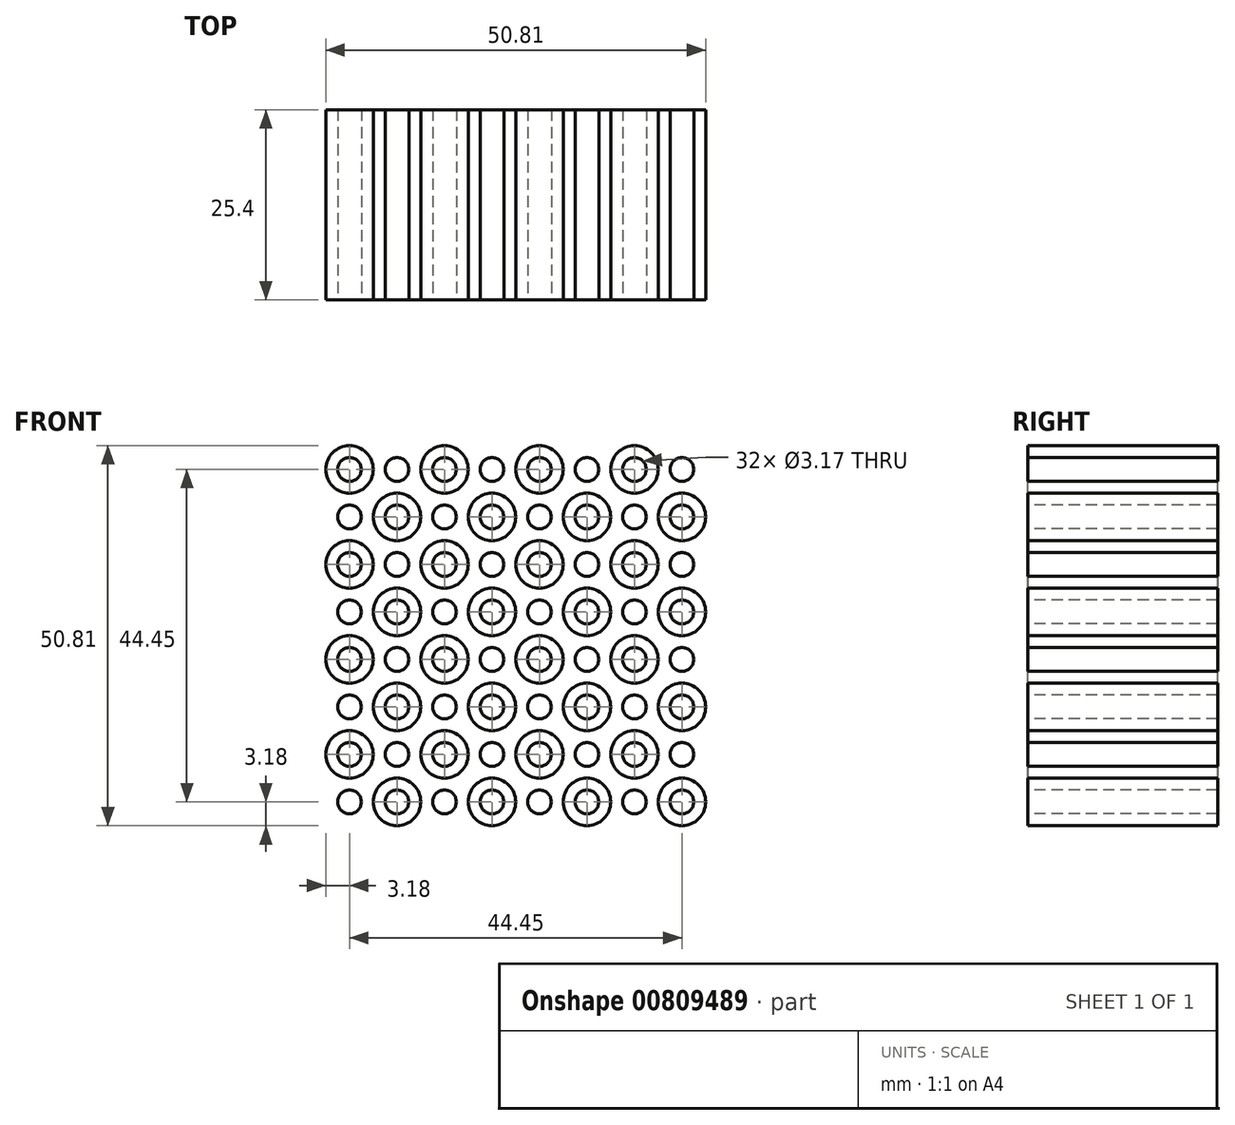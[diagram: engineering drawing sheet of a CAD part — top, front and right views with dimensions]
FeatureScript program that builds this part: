
annotation { "Feature Type Name" : "Feature", "Feature Type Description" : "" }
export const myFeature = defineFeature(function(context is Context, id is Id, definition is map)
    precondition{}
    {
        {
            var Q0;
            Q0=qCreatedBy(makeId("Front.planeOp"),FACE);
            var sketch = newSketch(context, id + "F0", { "sketchPlane" : qUnion([Q0])});
            skCircle(sketch, "E0", {"center": v(0, 0) * mm, "radius": 1.59 * mm});
            skCircle(sketch, "E1", {"center": v(0, 0) * mm, "radius": 3.18 * mm});
            skLineSegment(sketch, "E2.bottom", {"start": v(-3.18, 3.18) * mm, "end": v(3.18, 3.18) * mm});
            skLineSegment(sketch, "E2.top", {"start": v(-3.17, -3.18) * mm, "end": v(3.18, -3.18) * mm});
            skLineSegment(sketch, "E2.left", {"start": v(-3.18, 3.17) * mm, "end": v(-3.18, -3.18) * mm});
            skLineSegment(sketch, "E2.right", {"start": v(3.18, 3.18) * mm, "end": v(3.18, -3.18) * mm});
            skCircle(sketch, "E3.MirrorC", {"center": v(6.35, 0) * mm, "radius": 3.18 * mm});
            skCircle(sketch, "E4.MirrorC", {"center": v(6.35, 0) * mm, "radius": 1.59 * mm});
            skLineSegment(sketch, "E5.MirrorCS", {"start": v(9.53, 3.18) * mm, "end": v(3.17, 3.18) * mm});
            skLineSegment(sketch, "E6.MirrorCS", {"start": v(9.53, 3.18) * mm, "end": v(9.53, -3.17) * mm});
            skLineSegment(sketch, "E7.MirrorCS", {"start": v(9.53, -3.17) * mm, "end": v(3.17, -3.18) * mm});
            skCircle(sketch, "E8.MirrorC", {"center": v(6.35, -6.35) * mm, "radius": 3.18 * mm});
            skCircle(sketch, "E9.MirrorC", {"center": v(0, -6.35) * mm, "radius": 3.18 * mm});
            skCircle(sketch, "E10.MirrorC", {"center": v(0, -6.35) * mm, "radius": 1.59 * mm});
            skLineSegment(sketch, "E11.MirrorCS", {"start": v(3.18, -9.53) * mm, "end": v(3.18, -3.18) * mm});
            skCircle(sketch, "E12.MirrorC", {"center": v(6.35, -6.35) * mm, "radius": 1.59 * mm});
            skCircle(sketch, "E13.MirrorC", {"center": v(-6.35, 0) * mm, "radius": 1.59 * mm});
            skCircle(sketch, "E14.MirrorC", {"center": v(-6.35, 0) * mm, "radius": 3.18 * mm});
            skCircle(sketch, "E15.MirrorC", {"center": v(-12.7, 0) * mm, "radius": 3.18 * mm});
            skCircle(sketch, "E16.MirrorC", {"center": v(-12.7, 0) * mm, "radius": 1.59 * mm});
            skLineSegment(sketch, "E17.MirrorCS", {"start": v(-9.53, 3.17) * mm, "end": v(-9.53, -3.18) * mm});
            skLineSegment(sketch, "E18.MirrorCS", {"start": v(-3.18, 3.18) * mm, "end": v(-9.53, 3.17) * mm});
            skCircle(sketch, "E19.MirrorC", {"center": v(-6.35, -6.35) * mm, "radius": 1.59 * mm});
            skCircle(sketch, "E20.MirrorC", {"center": v(-6.35, -6.35) * mm, "radius": 3.18 * mm});
            skCircle(sketch, "E21.MirrorC", {"center": v(-12.7, -6.35) * mm, "radius": 1.59 * mm});
            skCircle(sketch, "E22.MirrorC", {"center": v(-12.7, -6.35) * mm, "radius": 3.18 * mm});
            skLineSegment(sketch, "E23.MirrorCS", {"start": v(-3.18, -9.53) * mm, "end": v(3.18, -9.53) * mm});
            skCircle(sketch, "E24.MirrorC", {"center": v(-12.7, -19.05) * mm, "radius": 3.18 * mm});
            skCircle(sketch, "E25.MirrorC", {"center": v(-12.7, -19.05) * mm, "radius": 1.59 * mm});
            skCircle(sketch, "E26.MirrorC", {"center": v(-6.35, -19.05) * mm, "radius": 1.59 * mm});
            skCircle(sketch, "E27.MirrorC", {"center": v(-6.35, -19.05) * mm, "radius": 3.18 * mm});
            skCircle(sketch, "E28.MirrorC", {"center": v(0, -19.05) * mm, "radius": 3.18 * mm});
            skCircle(sketch, "E29.MirrorC", {"center": v(0, -19.05) * mm, "radius": 1.59 * mm});
            skCircle(sketch, "E30.MirrorC", {"center": v(6.35, -19.05) * mm, "radius": 3.18 * mm});
            skCircle(sketch, "E31.MirrorC", {"center": v(6.35, -19.05) * mm, "radius": 1.59 * mm});
            skLineSegment(sketch, "E32.MirrorCS", {"start": v(-3.18, -22.23) * mm, "end": v(3.18, -22.23) * mm});
            skCircle(sketch, "E33.MirrorC", {"center": v(-12.7, -12.7) * mm, "radius": 1.59 * mm});
            skCircle(sketch, "E34.MirrorC", {"center": v(-12.7, -12.7) * mm, "radius": 3.18 * mm});
            skCircle(sketch, "E35.MirrorC", {"center": v(-6.35, -12.7) * mm, "radius": 3.18 * mm});
            skCircle(sketch, "E36.MirrorC", {"center": v(-6.35, -12.7) * mm, "radius": 1.59 * mm});
            skCircle(sketch, "E37.MirrorC", {"center": v(0, -12.7) * mm, "radius": 1.59 * mm});
            skCircle(sketch, "E38.MirrorC", {"center": v(0, -12.7) * mm, "radius": 3.18 * mm});
            skCircle(sketch, "E39.MirrorC", {"center": v(6.35, -12.7) * mm, "radius": 3.18 * mm});
            skCircle(sketch, "E40.MirrorC", {"center": v(6.35, -12.7) * mm, "radius": 1.59 * mm});
            skCircle(sketch, "E41.MirrorC", {"center": v(31.75, 0) * mm, "radius": 3.18 * mm});
            skCircle(sketch, "E42.MirrorC", {"center": v(31.75, 0) * mm, "radius": 1.59 * mm});
            skCircle(sketch, "E43.MirrorC", {"center": v(25.4, 0) * mm, "radius": 1.59 * mm});
            skCircle(sketch, "E44.MirrorC", {"center": v(25.4, 0) * mm, "radius": 3.18 * mm});
            skCircle(sketch, "E45.MirrorC", {"center": v(19.05, 0) * mm, "radius": 3.18 * mm});
            skCircle(sketch, "E46.MirrorC", {"center": v(19.05, 0) * mm, "radius": 1.59 * mm});
            skCircle(sketch, "E47.MirrorC", {"center": v(12.7, 0) * mm, "radius": 3.18 * mm});
            skCircle(sketch, "E48.MirrorC", {"center": v(12.7, 0) * mm, "radius": 1.59 * mm});
            skCircle(sketch, "E49.MirrorC", {"center": v(12.7, -6.35) * mm, "radius": 1.59 * mm});
            skCircle(sketch, "E50.MirrorC", {"center": v(12.7, -6.35) * mm, "radius": 3.18 * mm});
            skCircle(sketch, "E51.MirrorC", {"center": v(19.05, -6.35) * mm, "radius": 3.18 * mm});
            skCircle(sketch, "E52.MirrorC", {"center": v(19.05, -6.35) * mm, "radius": 1.59 * mm});
            skCircle(sketch, "E53.MirrorC", {"center": v(25.4, -12.7) * mm, "radius": 3.18 * mm});
            skCircle(sketch, "E54.MirrorC", {"center": v(25.4, -12.7) * mm, "radius": 1.59 * mm});
            skCircle(sketch, "E55.MirrorC", {"center": v(25.4, -6.35) * mm, "radius": 3.18 * mm});
            skCircle(sketch, "E56.MirrorC", {"center": v(25.4, -6.35) * mm, "radius": 1.59 * mm});
            skCircle(sketch, "E57.MirrorC", {"center": v(31.75, -6.35) * mm, "radius": 1.59 * mm});
            skCircle(sketch, "E58.MirrorC", {"center": v(31.75, -6.35) * mm, "radius": 3.18 * mm});
            skCircle(sketch, "E59.MirrorC", {"center": v(31.75, -12.7) * mm, "radius": 3.18 * mm});
            skCircle(sketch, "E60.MirrorC", {"center": v(31.75, -12.7) * mm, "radius": 1.59 * mm});
            skCircle(sketch, "E61.MirrorC", {"center": v(31.75, -19.05) * mm, "radius": 3.18 * mm});
            skCircle(sketch, "E62.MirrorC", {"center": v(31.75, -19.05) * mm, "radius": 1.59 * mm});
            skCircle(sketch, "E63.MirrorC", {"center": v(25.4, -19.05) * mm, "radius": 1.59 * mm});
            skCircle(sketch, "E64.MirrorC", {"center": v(25.4, -19.05) * mm, "radius": 3.18 * mm});
            skCircle(sketch, "E65.MirrorC", {"center": v(19.05, -19.05) * mm, "radius": 3.18 * mm});
            skCircle(sketch, "E66.MirrorC", {"center": v(19.05, -19.05) * mm, "radius": 1.59 * mm});
            skCircle(sketch, "E67.MirrorC", {"center": v(12.7, -19.05) * mm, "radius": 3.18 * mm});
            skCircle(sketch, "E68.MirrorC", {"center": v(12.7, -19.05) * mm, "radius": 1.59 * mm});
            skCircle(sketch, "E69.MirrorC", {"center": v(12.7, -12.7) * mm, "radius": 3.18 * mm});
            skCircle(sketch, "E70.MirrorC", {"center": v(12.7, -12.7) * mm, "radius": 1.59 * mm});
            skCircle(sketch, "E71.MirrorC", {"center": v(19.05, -12.7) * mm, "radius": 3.18 * mm});
            skCircle(sketch, "E72.MirrorC", {"center": v(19.05, -12.7) * mm, "radius": 1.59 * mm});
            skCircle(sketch, "E73.MirrorC", {"center": v(-12.7, 6.35) * mm, "radius": 3.18 * mm});
            skCircle(sketch, "E74.MirrorC", {"center": v(-12.7, 6.35) * mm, "radius": 1.59 * mm});
            skCircle(sketch, "E75.MirrorC", {"center": v(31.75, 12.7) * mm, "radius": 3.18 * mm});
            skCircle(sketch, "E76.MirrorC", {"center": v(19.05, 19.05) * mm, "radius": 3.18 * mm});
            skCircle(sketch, "E77.MirrorC", {"center": v(12.7, 12.7) * mm, "radius": 1.59 * mm});
            skCircle(sketch, "E78.MirrorC", {"center": v(-6.35, 25.4) * mm, "radius": 3.18 * mm});
            skCircle(sketch, "E79.MirrorC", {"center": v(-6.35, 19.05) * mm, "radius": 1.59 * mm});
            skCircle(sketch, "E80.MirrorC", {"center": v(-6.35, 12.7) * mm, "radius": 3.18 * mm});
            skCircle(sketch, "E81.MirrorC", {"center": v(-6.35, 19.05) * mm, "radius": 3.18 * mm});
            skCircle(sketch, "E82.MirrorC", {"center": v(-12.7, 12.7) * mm, "radius": 3.18 * mm});
            skCircle(sketch, "E83.MirrorC", {"center": v(-6.35, 12.7) * mm, "radius": 1.59 * mm});
            skCircle(sketch, "E84.MirrorC", {"center": v(0, 19.05) * mm, "radius": 1.59 * mm});
            skCircle(sketch, "E85.MirrorC", {"center": v(0, 12.7) * mm, "radius": 1.59 * mm});
            skCircle(sketch, "E86.MirrorC", {"center": v(19.05, 12.7) * mm, "radius": 1.59 * mm});
            skCircle(sketch, "E87.MirrorC", {"center": v(0, 12.7) * mm, "radius": 3.18 * mm});
            skCircle(sketch, "E88.MirrorC", {"center": v(6.35, 19.05) * mm, "radius": 3.18 * mm});
            skCircle(sketch, "E89.MirrorC", {"center": v(12.7, 12.7) * mm, "radius": 3.18 * mm});
            skCircle(sketch, "E90.MirrorC", {"center": v(25.4, 12.7) * mm, "radius": 1.59 * mm});
            skCircle(sketch, "E91.MirrorC", {"center": v(6.35, 12.7) * mm, "radius": 1.59 * mm});
            skCircle(sketch, "E92.MirrorC", {"center": v(-12.7, 19.05) * mm, "radius": 1.59 * mm});
            skCircle(sketch, "E93.MirrorC", {"center": v(-12.7, 25.4) * mm, "radius": 1.59 * mm});
            skCircle(sketch, "E94.MirrorC", {"center": v(-12.7, 25.4) * mm, "radius": 3.18 * mm});
            skCircle(sketch, "E95.MirrorC", {"center": v(-12.7, 19.05) * mm, "radius": 3.18 * mm});
            skCircle(sketch, "E96.MirrorC", {"center": v(-12.7, 12.7) * mm, "radius": 1.59 * mm});
            skCircle(sketch, "E97.MirrorC", {"center": v(-6.35, 25.4) * mm, "radius": 1.59 * mm});
            skCircle(sketch, "E98.MirrorC", {"center": v(-6.35, 6.35) * mm, "radius": 3.18 * mm});
            skCircle(sketch, "E99.MirrorC", {"center": v(-6.35, 6.35) * mm, "radius": 1.59 * mm});
            skCircle(sketch, "E100.MirrorC", {"center": v(0, 6.35) * mm, "radius": 1.59 * mm});
            skCircle(sketch, "E101.MirrorC", {"center": v(0, 6.35) * mm, "radius": 3.18 * mm});
            skCircle(sketch, "E102.MirrorC", {"center": v(0, 19.05) * mm, "radius": 3.18 * mm});
            skCircle(sketch, "E103.MirrorC", {"center": v(0, 25.4) * mm, "radius": 3.18 * mm});
            skCircle(sketch, "E104.MirrorC", {"center": v(0, 25.4) * mm, "radius": 1.59 * mm});
            skCircle(sketch, "E105.MirrorC", {"center": v(6.35, 25.4) * mm, "radius": 3.18 * mm});
            skCircle(sketch, "E106.MirrorC", {"center": v(6.35, 25.4) * mm, "radius": 1.59 * mm});
            skCircle(sketch, "E107.MirrorC", {"center": v(6.35, 19.05) * mm, "radius": 1.59 * mm});
            skCircle(sketch, "E108.MirrorC", {"center": v(6.35, 12.7) * mm, "radius": 3.18 * mm});
            skCircle(sketch, "E109.MirrorC", {"center": v(6.35, 6.35) * mm, "radius": 3.18 * mm});
            skCircle(sketch, "E110.MirrorC", {"center": v(6.35, 6.35) * mm, "radius": 1.59 * mm});
            skCircle(sketch, "E111.MirrorC", {"center": v(12.7, 6.35) * mm, "radius": 3.18 * mm});
            skCircle(sketch, "E112.MirrorC", {"center": v(12.7, 6.35) * mm, "radius": 1.59 * mm});
            skCircle(sketch, "E113.MirrorC", {"center": v(25.4, 12.7) * mm, "radius": 3.18 * mm});
            skCircle(sketch, "E114.MirrorC", {"center": v(19.05, 12.7) * mm, "radius": 3.18 * mm});
            skCircle(sketch, "E115.MirrorC", {"center": v(19.05, 6.35) * mm, "radius": 1.59 * mm});
            skCircle(sketch, "E116.MirrorC", {"center": v(19.05, 6.35) * mm, "radius": 3.18 * mm});
            skCircle(sketch, "E117.MirrorC", {"center": v(25.4, 6.35) * mm, "radius": 3.18 * mm});
            skCircle(sketch, "E118.MirrorC", {"center": v(25.4, 6.35) * mm, "radius": 1.59 * mm});
            skCircle(sketch, "E119.MirrorC", {"center": v(31.75, 6.35) * mm, "radius": 3.18 * mm});
            skCircle(sketch, "E120.MirrorC", {"center": v(31.75, 6.35) * mm, "radius": 1.59 * mm});
            skCircle(sketch, "E121.MirrorC", {"center": v(31.75, 25.4) * mm, "radius": 3.18 * mm});
            skCircle(sketch, "E122.MirrorC", {"center": v(25.4, 25.4) * mm, "radius": 3.18 * mm});
            skCircle(sketch, "E123.MirrorC", {"center": v(19.05, 25.4) * mm, "radius": 3.18 * mm});
            skCircle(sketch, "E124.MirrorC", {"center": v(12.7, 25.4) * mm, "radius": 3.18 * mm});
            skCircle(sketch, "E125.MirrorC", {"center": v(12.7, 25.4) * mm, "radius": 1.59 * mm});
            skCircle(sketch, "E126.MirrorC", {"center": v(19.05, 25.4) * mm, "radius": 1.59 * mm});
            skCircle(sketch, "E127.MirrorC", {"center": v(25.4, 25.4) * mm, "radius": 1.59 * mm});
            skCircle(sketch, "E128.MirrorC", {"center": v(31.75, 25.4) * mm, "radius": 1.59 * mm});
            skCircle(sketch, "E129.MirrorC", {"center": v(12.7, 19.05) * mm, "radius": 3.18 * mm});
            skCircle(sketch, "E130.MirrorC", {"center": v(12.7, 19.05) * mm, "radius": 1.59 * mm});
            skCircle(sketch, "E131.MirrorC", {"center": v(19.05, 19.05) * mm, "radius": 1.59 * mm});
            skCircle(sketch, "E132.MirrorC", {"center": v(25.4, 19.05) * mm, "radius": 3.18 * mm});
            skCircle(sketch, "E133.MirrorC", {"center": v(31.75, 19.05) * mm, "radius": 3.18 * mm});
            skCircle(sketch, "E134.MirrorC", {"center": v(31.75, 12.7) * mm, "radius": 1.59 * mm});
            skCircle(sketch, "E135.MirrorC", {"center": v(31.75, 19.05) * mm, "radius": 1.59 * mm});
            skCircle(sketch, "E136.MirrorC", {"center": v(25.4, 19.05) * mm, "radius": 1.59 * mm});
            skSolve(sketch);
        }
        {
            var Q0;
            Q0=makeQuery(id+"F0.imprint","IMPRINT",FACE,{"disambiguationData":[TD([[makeQuery(id+"F0.imprint","IMPRINT",EDGE,{"derivedFrom":sQuery(id+"F0.wireOp",EDGE,"E97.MirrorC")}),1.0]])]});
            var Q1;
            Q1=makeQuery(id+"F0.imprint","IMPRINT",FACE,{"disambiguationData":[TD([[makeQuery(id+"F0.imprint","IMPRINT",EDGE,{"derivedFrom":sQuery(id+"F0.wireOp",EDGE,"E104.MirrorC")}),-1.0]])]});
            var Q2;
            Q2=makeQuery(id+"F0.imprint","IMPRINT",FACE,{"disambiguationData":[TD([[makeQuery(id+"F0.imprint","IMPRINT",EDGE,{"derivedFrom":sQuery(id+"F0.wireOp",EDGE,"E106.MirrorC")}),1.0]])]});
            var Q3;
            Q3=makeQuery(id+"F0.imprint","IMPRINT",FACE,{"disambiguationData":[TD([[makeQuery(id+"F0.imprint","IMPRINT",EDGE,{"derivedFrom":sQuery(id+"F0.wireOp",EDGE,"E125.MirrorC")}),-1.0]])]});
            var Q4;
            Q4=makeQuery(id+"F0.imprint","IMPRINT",FACE,{"disambiguationData":[TD([[makeQuery(id+"F0.imprint","IMPRINT",EDGE,{"derivedFrom":sQuery(id+"F0.wireOp",EDGE,"E93.MirrorC")}),-1.0]])]});
            var Q5;
            Q5=makeQuery(id+"F0.imprint","IMPRINT",FACE,{"disambiguationData":[TD([[makeQuery(id+"F0.imprint","IMPRINT",EDGE,{"derivedFrom":sQuery(id+"F0.wireOp",EDGE,"E126.MirrorC")}),1.0]])]});
            var Q6;
            Q6=makeQuery(id+"F0.imprint","IMPRINT",FACE,{"disambiguationData":[TD([[makeQuery(id+"F0.imprint","IMPRINT",EDGE,{"derivedFrom":sQuery(id+"F0.wireOp",EDGE,"E127.MirrorC")}),-1.0]])]});
            var Q7;
            Q7=makeQuery(id+"F0.imprint","IMPRINT",FACE,{"disambiguationData":[TD([[makeQuery(id+"F0.imprint","IMPRINT",EDGE,{"derivedFrom":sQuery(id+"F0.wireOp",EDGE,"E128.MirrorC")}),1.0]])]});
            var Q8;
            Q8=makeQuery(id+"F0.imprint","IMPRINT",FACE,{"disambiguationData":[TD([[makeQuery(id+"F0.imprint","IMPRINT",EDGE,{"derivedFrom":sQuery(id+"F0.wireOp",EDGE,"E135.MirrorC")}),-1.0]])]});
            var Q9;
            Q9=makeQuery(id+"F0.imprint","IMPRINT",FACE,{"disambiguationData":[TD([[makeQuery(id+"F0.imprint","IMPRINT",EDGE,{"derivedFrom":sQuery(id+"F0.wireOp",EDGE,"E136.MirrorC")}),1.0]])]});
            var Q10;
            Q10=makeQuery(id+"F0.imprint","IMPRINT",FACE,{"disambiguationData":[TD([[makeQuery(id+"F0.imprint","IMPRINT",EDGE,{"derivedFrom":sQuery(id+"F0.wireOp",EDGE,"E131.MirrorC")}),-1.0]])]});
            var Q11;
            Q11=makeQuery(id+"F0.imprint","IMPRINT",FACE,{"disambiguationData":[TD([[makeQuery(id+"F0.imprint","IMPRINT",EDGE,{"derivedFrom":sQuery(id+"F0.wireOp",EDGE,"E130.MirrorC")}),1.0]])]});
            var Q12;
            Q12=makeQuery(id+"F0.imprint","IMPRINT",FACE,{"disambiguationData":[TD([[makeQuery(id+"F0.imprint","IMPRINT",EDGE,{"derivedFrom":sQuery(id+"F0.wireOp",EDGE,"E107.MirrorC")}),-1.0]])]});
            var Q13;
            Q13=makeQuery(id+"F0.imprint","IMPRINT",FACE,{"disambiguationData":[TD([[makeQuery(id+"F0.imprint","IMPRINT",EDGE,{"derivedFrom":sQuery(id+"F0.wireOp",EDGE,"E84.MirrorC")}),1.0]])]});
            var Q14;
            Q14=makeQuery(id+"F0.imprint","IMPRINT",FACE,{"disambiguationData":[TD([[makeQuery(id+"F0.imprint","IMPRINT",EDGE,{"derivedFrom":sQuery(id+"F0.wireOp",EDGE,"E79.MirrorC")}),-1.0]])]});
            var Q15;
            Q15=makeQuery(id+"F0.imprint","IMPRINT",FACE,{"disambiguationData":[TD([[makeQuery(id+"F0.imprint","IMPRINT",EDGE,{"derivedFrom":sQuery(id+"F0.wireOp",EDGE,"E92.MirrorC")}),1.0]])]});
            var Q16;
            Q16=makeQuery(id+"F0.imprint","IMPRINT",FACE,{"disambiguationData":[TD([[makeQuery(id+"F0.imprint","IMPRINT",EDGE,{"derivedFrom":sQuery(id+"F0.wireOp",EDGE,"E96.MirrorC")}),-1.0]])]});
            var Q17;
            Q17=makeQuery(id+"F0.imprint","IMPRINT",FACE,{"disambiguationData":[TD([[makeQuery(id+"F0.imprint","IMPRINT",EDGE,{"derivedFrom":sQuery(id+"F0.wireOp",EDGE,"E83.MirrorC")}),1.0]])]});
            var Q18;
            Q18=makeQuery(id+"F0.imprint","IMPRINT",FACE,{"disambiguationData":[TD([[makeQuery(id+"F0.imprint","IMPRINT",EDGE,{"derivedFrom":sQuery(id+"F0.wireOp",EDGE,"E91.MirrorC")}),1.0]])]});
            var Q19;
            Q19=makeQuery(id+"F0.imprint","IMPRINT",FACE,{"disambiguationData":[TD([[makeQuery(id+"F0.imprint","IMPRINT",EDGE,{"derivedFrom":sQuery(id+"F0.wireOp",EDGE,"E77.MirrorC")}),-1.0]])]});
            var Q20;
            Q20=makeQuery(id+"F0.imprint","IMPRINT",FACE,{"disambiguationData":[TD([[makeQuery(id+"F0.imprint","IMPRINT",EDGE,{"derivedFrom":sQuery(id+"F0.wireOp",EDGE,"E86.MirrorC")}),1.0]])]});
            var Q21;
            Q21=makeQuery(id+"F0.imprint","IMPRINT",FACE,{"disambiguationData":[TD([[makeQuery(id+"F0.imprint","IMPRINT",EDGE,{"derivedFrom":sQuery(id+"F0.wireOp",EDGE,"E90.MirrorC")}),-1.0]])]});
            var Q22;
            Q22=makeQuery(id+"F0.imprint","IMPRINT",FACE,{"disambiguationData":[TD([[makeQuery(id+"F0.imprint","IMPRINT",EDGE,{"derivedFrom":sQuery(id+"F0.wireOp",EDGE,"E134.MirrorC")}),1.0]])]});
            var Q23;
            Q23=makeQuery(id+"F0.imprint","IMPRINT",FACE,{"disambiguationData":[TD([[makeQuery(id+"F0.imprint","IMPRINT",EDGE,{"derivedFrom":sQuery(id+"F0.wireOp",EDGE,"E118.MirrorC")}),1.0]])]});
            var Q24;
            Q24=makeQuery(id+"F0.imprint","IMPRINT",FACE,{"disambiguationData":[TD([[makeQuery(id+"F0.imprint","IMPRINT",EDGE,{"derivedFrom":sQuery(id+"F0.wireOp",EDGE,"E115.MirrorC")}),-1.0]])]});
            var Q25;
            Q25=makeQuery(id+"F0.imprint","IMPRINT",FACE,{"disambiguationData":[TD([[makeQuery(id+"F0.imprint","IMPRINT",EDGE,{"derivedFrom":sQuery(id+"F0.wireOp",EDGE,"E112.MirrorC")}),1.0]])]});
            var Q26;
            Q26=makeQuery(id+"F0.imprint","IMPRINT",FACE,{"disambiguationData":[TD([[makeQuery(id+"F0.imprint","IMPRINT",EDGE,{"derivedFrom":sQuery(id+"F0.wireOp",EDGE,"E110.MirrorC")}),-1.0]])]});
            var Q27;
            Q27=makeQuery(id+"F0.imprint","IMPRINT",FACE,{"disambiguationData":[TD([[makeQuery(id+"F0.imprint","IMPRINT",EDGE,{"derivedFrom":sQuery(id+"F0.wireOp",EDGE,"E100.MirrorC")}),1.0]])]});
            var Q28;
            Q28=makeQuery(id+"F0.imprint","IMPRINT",FACE,{"disambiguationData":[TD([[makeQuery(id+"F0.imprint","IMPRINT",EDGE,{"derivedFrom":sQuery(id+"F0.wireOp",EDGE,"E85.MirrorC")}),-1.0]])]});
            var Q29;
            Q29=makeQuery(id+"F0.imprint","IMPRINT",FACE,{"disambiguationData":[TD([[makeQuery(id+"F0.imprint","IMPRINT",EDGE,{"derivedFrom":sQuery(id+"F0.wireOp",EDGE,"E99.MirrorC")}),-1.0]])]});
            var Q30;
            Q30=makeQuery(id+"F0.imprint","IMPRINT",FACE,{"disambiguationData":[TD([[makeQuery(id+"F0.imprint","IMPRINT",EDGE,{"derivedFrom":sQuery(id+"F0.wireOp",EDGE,"E74.MirrorC")}),1.0]])]});
            var Q31;
            Q31=makeQuery(id+"F0.imprint","IMPRINT",FACE,{"disambiguationData":[TD([[makeQuery(id+"F0.imprint","IMPRINT",EDGE,{"derivedFrom":sQuery(id+"F0.wireOp",EDGE,"E120.MirrorC")}),-1.0]])]});
            var Q32;
            Q32=makeQuery(id+"F0.imprint","IMPRINT",FACE,{"disambiguationData":[TD([[makeQuery(id+"F0.imprint","IMPRINT",EDGE,{"derivedFrom":sQuery(id+"F0.wireOp",EDGE,"E42.MirrorC")}),1.0]])]});
            var Q33;
            Q33=makeQuery(id+"F0.imprint","IMPRINT",FACE,{"disambiguationData":[TD([[makeQuery(id+"F0.imprint","IMPRINT",EDGE,{"derivedFrom":sQuery(id+"F0.wireOp",EDGE,"E43.MirrorC")}),-1.0]])]});
            var Q34;
            Q34=makeQuery(id+"F0.imprint","IMPRINT",FACE,{"disambiguationData":[TD([[makeQuery(id+"F0.imprint","IMPRINT",EDGE,{"derivedFrom":sQuery(id+"F0.wireOp",EDGE,"E46.MirrorC")}),1.0]])]});
            var Q35;
            Q35=makeQuery(id+"F0.imprint","IMPRINT",FACE,{"disambiguationData":[TD([[makeQuery(id+"F0.imprint","IMPRINT",EDGE,{"derivedFrom":sQuery(id+"F0.wireOp",EDGE,"E48.MirrorC")}),-1.0]])]});
            var Q36;
            Q36=makeQuery(id+"F0.imprint","IMPRINT",FACE,{"disambiguationData":[TD([[makeQuery(id+"F0.imprint","IMPRINT",EDGE,{"derivedFrom":sQuery(id+"F0.wireOp",EDGE,"E4.MirrorC")}),1.0]])]});
            var Q37;
            Q37=makeQuery(id+"F0.imprint","IMPRINT",FACE,{"disambiguationData":[TD([[makeQuery(id+"F0.imprint","IMPRINT",EDGE,{"derivedFrom":sQuery(id+"F0.wireOp",EDGE,"E0")}),-1.0]])]});
            var Q38;
            Q38=makeQuery(id+"F0.imprint","IMPRINT",FACE,{"disambiguationData":[TD([[makeQuery(id+"F0.imprint","IMPRINT",EDGE,{"derivedFrom":sQuery(id+"F0.wireOp",EDGE,"E13.MirrorC")}),1.0]])]});
            var Q39;
            Q39=makeQuery(id+"F0.imprint","IMPRINT",FACE,{"disambiguationData":[TD([[makeQuery(id+"F0.imprint","IMPRINT",EDGE,{"derivedFrom":sQuery(id+"F0.wireOp",EDGE,"E16.MirrorC")}),-1.0]])]});
            var Q40;
            Q40=makeQuery(id+"F0.imprint","IMPRINT",FACE,{"disambiguationData":[TD([[makeQuery(id+"F0.imprint","IMPRINT",EDGE,{"derivedFrom":sQuery(id+"F0.wireOp",EDGE,"E21.MirrorC")}),1.0]])]});
            var Q41;
            Q41=makeQuery(id+"F0.imprint","IMPRINT",FACE,{"disambiguationData":[TD([[makeQuery(id+"F0.imprint","IMPRINT",EDGE,{"derivedFrom":sQuery(id+"F0.wireOp",EDGE,"E19.MirrorC")}),-1.0]])]});
            var Q42;
            Q42=makeQuery(id+"F0.imprint","IMPRINT",FACE,{"disambiguationData":[TD([[makeQuery(id+"F0.imprint","IMPRINT",EDGE,{"derivedFrom":sQuery(id+"F0.wireOp",EDGE,"E10.MirrorC")}),1.0]])]});
            var Q43;
            Q43=makeQuery(id+"F0.imprint","IMPRINT",FACE,{"disambiguationData":[TD([[makeQuery(id+"F0.imprint","IMPRINT",EDGE,{"derivedFrom":sQuery(id+"F0.wireOp",EDGE,"E12.MirrorC")}),-1.0]])]});
            var Q44;
            Q44=makeQuery(id+"F0.imprint","IMPRINT",FACE,{"disambiguationData":[TD([[makeQuery(id+"F0.imprint","IMPRINT",EDGE,{"derivedFrom":sQuery(id+"F0.wireOp",EDGE,"E49.MirrorC")}),1.0]])]});
            var Q45;
            Q45=makeQuery(id+"F0.imprint","IMPRINT",FACE,{"disambiguationData":[TD([[makeQuery(id+"F0.imprint","IMPRINT",EDGE,{"derivedFrom":sQuery(id+"F0.wireOp",EDGE,"E52.MirrorC")}),-1.0]])]});
            var Q46;
            Q46=makeQuery(id+"F0.imprint","IMPRINT",FACE,{"disambiguationData":[TD([[makeQuery(id+"F0.imprint","IMPRINT",EDGE,{"derivedFrom":sQuery(id+"F0.wireOp",EDGE,"E56.MirrorC")}),1.0]])]});
            var Q47;
            Q47=makeQuery(id+"F0.imprint","IMPRINT",FACE,{"disambiguationData":[TD([[makeQuery(id+"F0.imprint","IMPRINT",EDGE,{"derivedFrom":sQuery(id+"F0.wireOp",EDGE,"E57.MirrorC")}),-1.0]])]});
            var Q48;
            Q48=makeQuery(id+"F0.imprint","IMPRINT",FACE,{"disambiguationData":[TD([[makeQuery(id+"F0.imprint","IMPRINT",EDGE,{"derivedFrom":sQuery(id+"F0.wireOp",EDGE,"E33.MirrorC")}),-1.0]])]});
            var Q49;
            Q49=makeQuery(id+"F0.imprint","IMPRINT",FACE,{"disambiguationData":[TD([[makeQuery(id+"F0.imprint","IMPRINT",EDGE,{"derivedFrom":sQuery(id+"F0.wireOp",EDGE,"E37.MirrorC")}),-1.0]])]});
            var Q50;
            Q50=makeQuery(id+"F0.imprint","IMPRINT",FACE,{"disambiguationData":[TD([[makeQuery(id+"F0.imprint","IMPRINT",EDGE,{"derivedFrom":sQuery(id+"F0.wireOp",EDGE,"E40.MirrorC")}),1.0]])]});
            var Q51;
            Q51=makeQuery(id+"F0.imprint","IMPRINT",FACE,{"disambiguationData":[TD([[makeQuery(id+"F0.imprint","IMPRINT",EDGE,{"derivedFrom":sQuery(id+"F0.wireOp",EDGE,"E70.MirrorC")}),-1.0]])]});
            var Q52;
            Q52=makeQuery(id+"F0.imprint","IMPRINT",FACE,{"disambiguationData":[TD([[makeQuery(id+"F0.imprint","IMPRINT",EDGE,{"derivedFrom":sQuery(id+"F0.wireOp",EDGE,"E60.MirrorC")}),1.0]])]});
            var Q53;
            Q53=makeQuery(id+"F0.imprint","IMPRINT",FACE,{"disambiguationData":[TD([[makeQuery(id+"F0.imprint","IMPRINT",EDGE,{"derivedFrom":sQuery(id+"F0.wireOp",EDGE,"E54.MirrorC")}),-1.0]])]});
            var Q54;
            Q54=makeQuery(id+"F0.imprint","IMPRINT",FACE,{"disambiguationData":[TD([[makeQuery(id+"F0.imprint","IMPRINT",EDGE,{"derivedFrom":sQuery(id+"F0.wireOp",EDGE,"E36.MirrorC")}),1.0]])]});
            var Q55;
            Q55=makeQuery(id+"F0.imprint","IMPRINT",FACE,{"disambiguationData":[TD([[makeQuery(id+"F0.imprint","IMPRINT",EDGE,{"derivedFrom":sQuery(id+"F0.wireOp",EDGE,"E72.MirrorC")}),1.0]])]});
            var Q56;
            Q56=makeQuery(id+"F0.imprint","IMPRINT",FACE,{"disambiguationData":[TD([[makeQuery(id+"F0.imprint","IMPRINT",EDGE,{"derivedFrom":sQuery(id+"F0.wireOp",EDGE,"E25.MirrorC")}),1.0]])]});
            var Q57;
            Q57=makeQuery(id+"F0.imprint","IMPRINT",FACE,{"disambiguationData":[TD([[makeQuery(id+"F0.imprint","IMPRINT",EDGE,{"derivedFrom":sQuery(id+"F0.wireOp",EDGE,"E26.MirrorC")}),-1.0]])]});
            var Q58;
            Q58=makeQuery(id+"F0.imprint","IMPRINT",FACE,{"disambiguationData":[TD([[makeQuery(id+"F0.imprint","IMPRINT",EDGE,{"derivedFrom":sQuery(id+"F0.wireOp",EDGE,"E29.MirrorC")}),1.0]])]});
            var Q59;
            Q59=makeQuery(id+"F0.imprint","IMPRINT",FACE,{"disambiguationData":[TD([[makeQuery(id+"F0.imprint","IMPRINT",EDGE,{"derivedFrom":sQuery(id+"F0.wireOp",EDGE,"E31.MirrorC")}),-1.0]])]});
            var Q60;
            Q60=makeQuery(id+"F0.imprint","IMPRINT",FACE,{"disambiguationData":[TD([[makeQuery(id+"F0.imprint","IMPRINT",EDGE,{"derivedFrom":sQuery(id+"F0.wireOp",EDGE,"E68.MirrorC")}),1.0]])]});
            var Q61;
            Q61=makeQuery(id+"F0.imprint","IMPRINT",FACE,{"disambiguationData":[TD([[makeQuery(id+"F0.imprint","IMPRINT",EDGE,{"derivedFrom":sQuery(id+"F0.wireOp",EDGE,"E66.MirrorC")}),-1.0]])]});
            var Q62;
            Q62=makeQuery(id+"F0.imprint","IMPRINT",FACE,{"disambiguationData":[TD([[makeQuery(id+"F0.imprint","IMPRINT",EDGE,{"derivedFrom":sQuery(id+"F0.wireOp",EDGE,"E63.MirrorC")}),1.0]])]});
            var Q63;
            Q63=makeQuery(id+"F0.imprint","IMPRINT",FACE,{"disambiguationData":[TD([[makeQuery(id+"F0.imprint","IMPRINT",EDGE,{"derivedFrom":sQuery(id+"F0.wireOp",EDGE,"E62.MirrorC")}),-1.0]])]});
            extrude(context, id + "F1", {"entities" : qUnion([Q0, Q1, Q2, Q3, Q4, Q5, Q6, Q7, Q8, Q9, Q10, Q11, Q12, Q13, Q14, Q15, Q16, Q17, Q18, Q19, Q20, Q21, Q22, Q23, Q24, Q25, Q26, Q27, Q28, Q29, Q30, Q31, Q32, Q33, Q34, Q35, Q36, Q37, Q38, Q39, Q40, Q41, Q42, Q43, Q44, Q45, Q46, Q47, Q48, Q49, Q50, Q51, Q52, Q53, Q54, Q55, Q56, Q57, Q58, Q59, Q60, Q61, Q62, Q63]), "oppositeDirection" : true, "depth" : 25.4 * mm, "offsetDistance" : 25.4 * mm});
        }
    });
